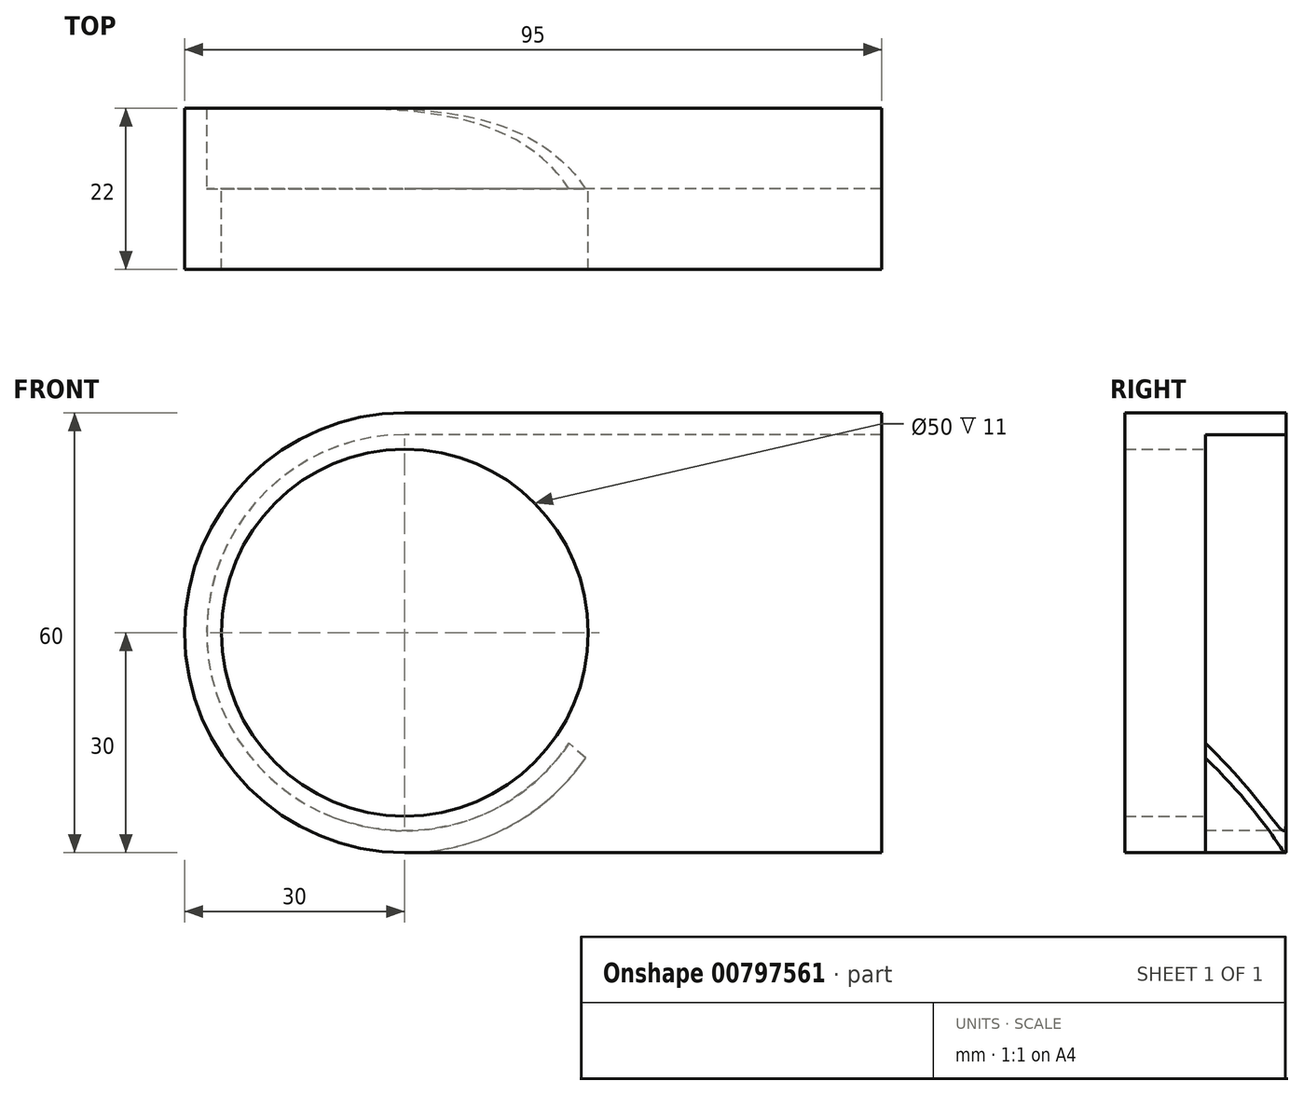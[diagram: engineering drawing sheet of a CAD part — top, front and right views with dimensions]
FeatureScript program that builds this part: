
annotation { "Feature Type Name" : "Feature", "Feature Type Description" : "" }
export const myFeature = defineFeature(function(context is Context, id is Id, definition is map)
    precondition{}
    {
        {
            var Q0;
            Q0=qCreatedBy(makeId("Front.planeOp"),FACE);
            var sketch = newSketch(context, id + "F0", { "sketchPlane" : qUnion([Q0])});
            skLineSegment(sketch, "E0.bottom", {"start": v(47.5, -30) * mm, "end": v(-17.5, -30) * mm});
            skLineSegment(sketch, "E0.top", {"start": v(47.5, 30) * mm, "end": v(-17.5, 30) * mm});
            skLineSegment(sketch, "E0.left", {"start": v(47.5, -30) * mm, "end": v(47.5, 30) * mm});
            skPoint(sketch, "E0.middle", {"position": v(0, 0) * mm});
            skCircle(sketch, "E1", {"center": v(-17.5, 0) * mm, "radius": 30 * mm});
            skPoint(sketch, "E1.first.point", {"position": v(-47.5, 0) * mm});
            skPoint(sketch, "E1.second.point", {"position": v(12.5, 0) * mm});
            skPoint(sketch, "E1.third.point", {"position": v(-17.5, -30) * mm});
            skPoint(sketch, "E2.orphan", {"position": v(-47.5, 30) * mm});
            skPoint(sketch, "E3.orphan", {"position": v(-47.5, -30) * mm});
            skCircle(sketch, "E4.0", {"center": v(-17.5, 0) * mm, "radius": 25 * mm});
            skSolve(sketch);
        }
        {
            var Q0;
            Q0=qSketchRegion(id+"F0",true);
            extrude(context, id + "F1", {"entities" : qUnion([Q0]), "depth" : 11 * mm, "offsetDistance" : 25 * mm});
        }
        {
            var Q0;
            Q0=makeQuery(id+"F1.opExtrude","CAP_FACE",FACE,{"disambiguationData":[OSD([sQuery(id+"F0.wireOp",EDGE,"E0.bottom"),sQuery(id+"F0.wireOp",EDGE,"E0.top"),sQuery(id+"F0.wireOp",EDGE,"E0.left"),sQuery(id+"F0.wireOp",EDGE,"E1"),sQuery(id+"F0.wireOp",EDGE,"E4.0")])],"isStart":true});
            var sketch = newSketch(context, id + "F2", { "sketchPlane" : qUnion([Q0])});
            skArc(sketch, "E5", {"start": v(17.5, -30) * mm, "mid": v(47.5, 0) * mm, "end": v(17.5, 30) * mm});
            skPoint(sketch, "E5.first.point", {"position": v(47.5, 0) * mm});
            skPoint(sketch, "E5.second.point", {"position": v(17.5, -30) * mm});
            skPoint(sketch, "E5.third.point", {"position": v(17.5, 30) * mm});
            skLineSegment(sketch, "E6.bottom", {"start": v(-47.5, 30) * mm, "end": v(17.51, 30) * mm});
            skLineSegment(sketch, "E6.top", {"start": v(-47.5, 27) * mm, "end": v(4.42, 27) * mm});
            skLineSegment(sketch, "E6.left", {"start": v(-47.5, 30) * mm, "end": v(-47.5, 27) * mm});
            skArc(sketch, "E7.0", {"start": v(-4.9, -15.08) * mm, "mid": v(41.34, -12.68) * mm, "end": v(17.5, 27) * mm});
            skLineSegment(sketch, "E8.trimOffspring", {"start": v(17.5, 27) * mm, "end": v(17.51, 27) * mm});
            skPoint(sketch, "E9.endSnap0", {"position": v(-15, -30) * mm});
            skLineSegment(sketch, "E10", {"start": v(4.42, 27) * mm, "end": v(17.51, 27) * mm});
            skArc(sketch, "E11", {"start": v(4.42, -27) * mm, "mid": v(10.8, -29.24) * mm, "end": v(17.5, -30) * mm});
            skPoint(sketch, "E9.end.orphan", {"position": v(-12.5, -30) * mm});
            skArc(sketch, "E12.trimOffspring", {"start": v(-7.14, -17.1) * mm, "mid": v(-2, -22.8) * mm, "end": v(4.42, -27) * mm});
            skLineSegment(sketch, "E13", {"start": v(-7.14, -17.1) * mm, "end": v(-4.9, -15.08) * mm});
            skSolve(sketch);
        }
        {
            var Q0;
            {var subQ5=sQuery(id+"F2.wireOp",EDGE,"E5");Q0=makeQuery(id+"F2.imprint","IMPRINT",FACE,{"disambiguationData":[TD([[makeQuery(id+"F2.imprint","IMPRINT",EDGE,{"derivedFrom":subQ5}),-1.0]])]});}
            extrude(context, id + "F3", {"entities" : qUnion([Q0]), "operationType" : NewBodyOperationType.ADD, "depth" : 11 * mm, "offsetDistance" : 25 * mm});
        }
        {
            var Q0;
            Q0=makeQuery(id+"F3.opExtrude","CAP_EDGE",EDGE,{"disambiguationData":[OSD([sQuery(id+"F2.wireOp",EDGE,"E13")])],"isStart":false});
            fillet(context, id + "F4", {"entities" : qUnion([Q0]), "radius" : 45 * mm, "tangentPropagation" : true, "allowEdgeOverflow" : false});
        }
    });
